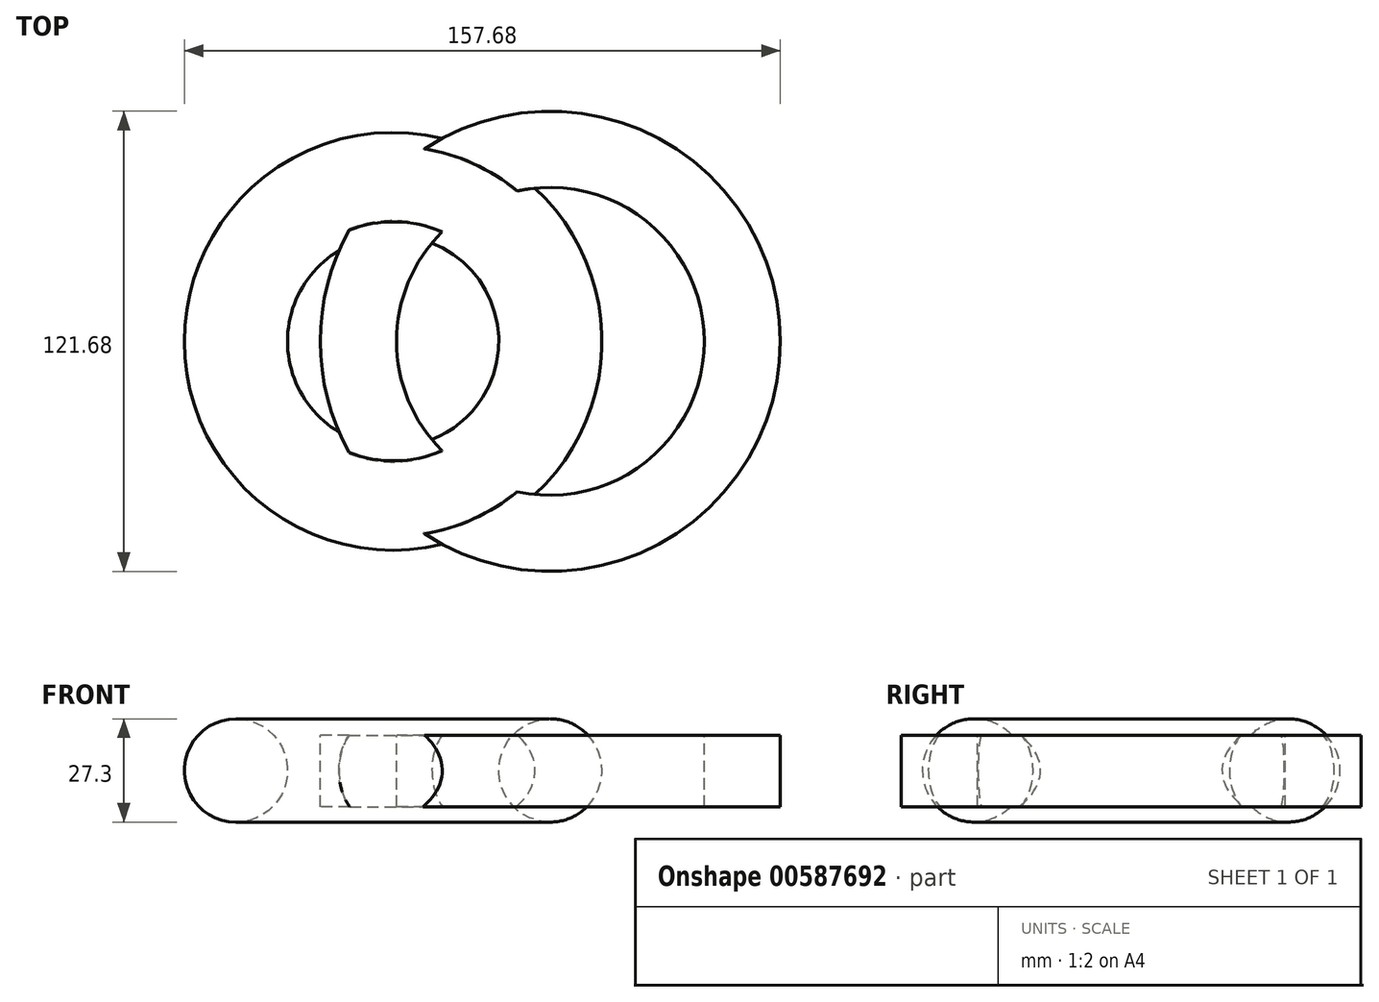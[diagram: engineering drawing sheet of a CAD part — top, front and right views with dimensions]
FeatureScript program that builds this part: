
annotation { "Feature Type Name" : "Feature", "Feature Type Description" : "" }
export const myFeature = defineFeature(function(context is Context, id is Id, definition is map)
    precondition{}
    {
        {
            var Q0;
            Q0=qCreatedBy(makeId("Front.planeOp"),FACE);
            var sketch = newSketch(context, id + "F0", { "sketchPlane" : qUnion([Q0])});
            skLineSegment(sketch, "E0", {"start": v(0, 74.75) * mm, "end": v(0, -54.62) * mm, "construction": true});
            skLineSegment(sketch, "E1.bottom", {"start": v(40.7, 9.33) * mm, "end": v(60.84, 9.33) * mm});
            skLineSegment(sketch, "E1.top", {"start": v(40.7, -9.62) * mm, "end": v(60.84, -9.62) * mm});
            skLineSegment(sketch, "E1.left", {"start": v(40.7, 9.33) * mm, "end": v(40.7, -9.62) * mm});
            skLineSegment(sketch, "E1.right", {"start": v(60.84, 9.33) * mm, "end": v(60.84, -9.62) * mm});
            skSolve(sketch);
        }
        {
            var Q0;
            Q0 = qSketchRegion(id + "F0", true);
            var Q1;
            Q1=sQuery(id+"F0.wireOp",EDGE,"E0");
            revolve(context, id + "F1", {"entities" : qUnion([Q0]), "axis" : qUnion([Q1]), "revolveType" : RevolveType.FULL});
        }
        {
            var Q0;
            Q0=qCreatedBy(makeId("Front.planeOp"),FACE);
            var sketch = newSketch(context, id + "F2", { "sketchPlane" : qUnion([Q0])});
            skLineSegment(sketch, "E2", {"start": v(-41.6, 71.8) * mm, "end": v(-41.6, -60.25) * mm});
            skCircle(sketch, "E3", {"center": v(0, 0) * mm, "radius": 13.65 * mm});
            skSolve(sketch);
        }
        {
            var Q0;
            Q0 = qSketchRegion(id + "F2", true);
            var Q1;
            Q1=sQuery(id+"F2.wireOp",EDGE,"E2");
            revolve(context, id + "F3", {"operationType" : NewBodyOperationType.ADD, "entities" : qUnion([Q0]), "axis" : qUnion([Q1]), "revolveType" : RevolveType.FULL});
        }
    });
